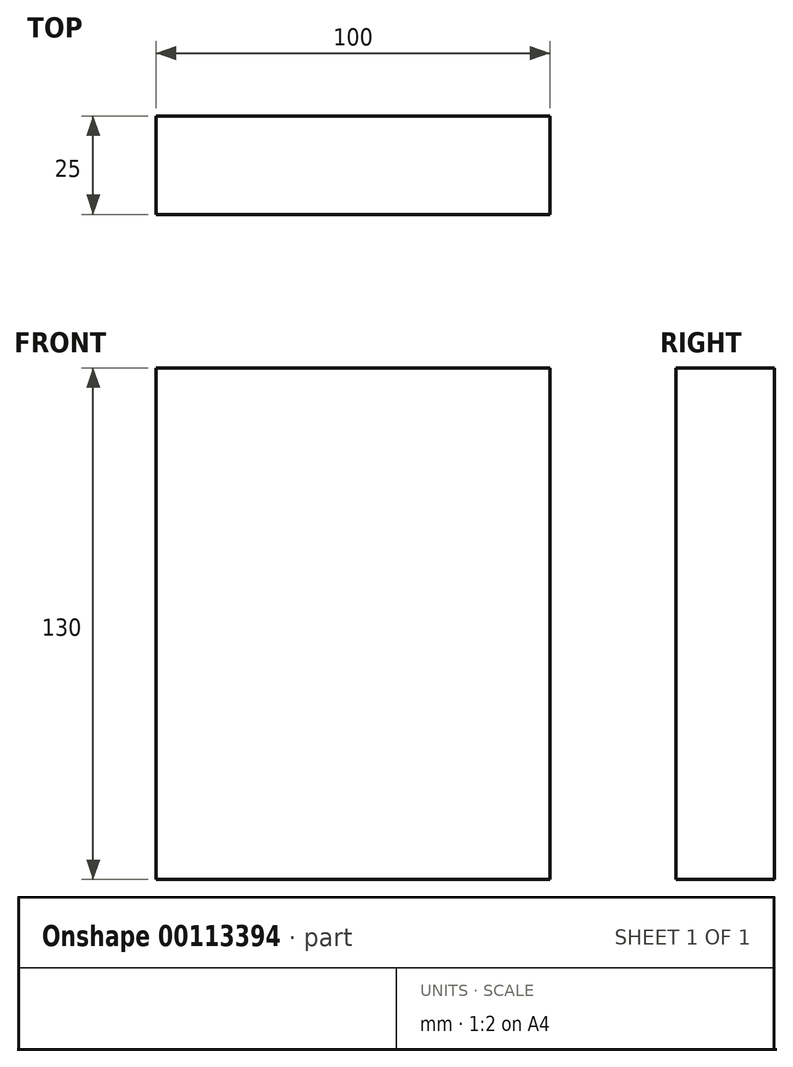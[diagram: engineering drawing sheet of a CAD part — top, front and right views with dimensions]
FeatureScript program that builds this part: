
annotation { "Feature Type Name" : "Feature", "Feature Type Description" : "" }
export const myFeature = defineFeature(function(context is Context, id is Id, definition is map)
    precondition{}
    {
        {
            var Q0;
            Q0=qCreatedBy(makeId("Front.planeOp"),FACE);
            var sketch = newSketch(context, id + "F0", { "sketchPlane" : qUnion([Q0])});
            skLineSegment(sketch, "E0", {"start": v(0, 0) * mm, "end": v(0, 130) * mm});
            skLineSegment(sketch, "E1", {"start": v(0, 130) * mm, "end": v(100, 130) * mm});
            skLineSegment(sketch, "E2", {"start": v(100, 130) * mm, "end": v(100, 0) * mm});
            skLineSegment(sketch, "E3", {"start": v(100, 0) * mm, "end": v(0, 0) * mm});
            skSolve(sketch);
        }
        {
            var Q0;
            Q0=makeQuery(id+"F0.imprint","IMPRINT",FACE,{"disambiguationData":[TD([[makeQuery(id+"F0.imprint","IMPRINT",EDGE,{"derivedFrom":sQuery(id+"F0.wireOp",EDGE,"E0")}),-1.0]])]});
            extrude(context, id + "F1", {"entities" : qUnion([Q0]), "depth" : 25 * mm});
        }
    });
